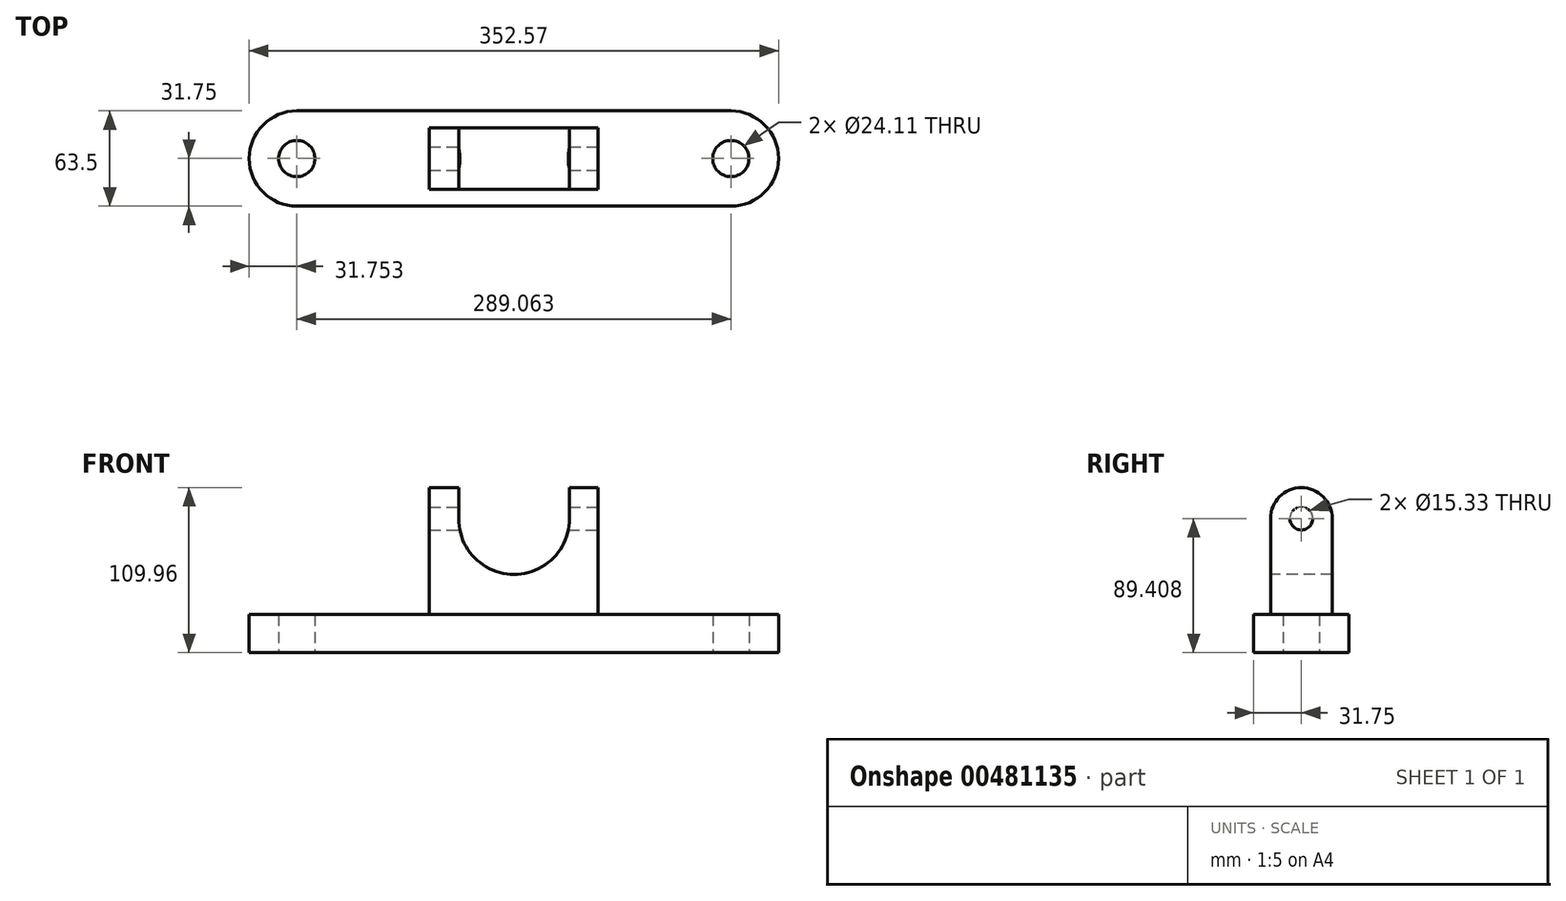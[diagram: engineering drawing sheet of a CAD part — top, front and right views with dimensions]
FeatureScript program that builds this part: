
annotation { "Feature Type Name" : "Feature", "Feature Type Description" : "" }
export const myFeature = defineFeature(function(context is Context, id is Id, definition is map)
    precondition{}
    {
        {
            var Q0;
            Q0=qCreatedBy(makeId("Top.planeOp"),FACE);
            var sketch = newSketch(context, id + "F0", { "sketchPlane" : qUnion([Q0])});
            skArc(sketch, "E0", {"start": v(-144.33, 31.75) * mm, "mid": v(-176.08, 0) * mm, "end": v(-144.33, -31.75) * mm});
            skCircle(sketch, "E1", {"center": v(-144.33, 0) * mm, "radius": 12.05 * mm});
            skArc(sketch, "E2", {"start": v(144.74, -31.75) * mm, "mid": v(176.49, 0) * mm, "end": v(144.74, 31.75) * mm});
            skCircle(sketch, "E3", {"center": v(144.74, 0) * mm, "radius": 12.05 * mm});
            skLineSegment(sketch, "E4", {"start": v(-144.33, 31.75) * mm, "end": v(144.74, 31.75) * mm});
            skLineSegment(sketch, "E5", {"start": v(-144.33, -31.75) * mm, "end": v(144.74, -31.75) * mm});
            skSolve(sketch);
        }
        {
            var Q0;
            Q0=qCreatedBy(makeId("Top.planeOp"),FACE);
            var sketch = newSketch(context, id + "F1", { "sketchPlane" : qUnion([Q0])});
            skLineSegment(sketch, "E6.bottom", {"start": v(56.16, -20.55) * mm, "end": v(-56.16, -20.55) * mm});
            skLineSegment(sketch, "E6.top", {"start": v(56.16, 20.55) * mm, "end": v(-56.16, 20.55) * mm});
            skLineSegment(sketch, "E6.left", {"start": v(56.16, -20.55) * mm, "end": v(56.16, 20.55) * mm});
            skLineSegment(sketch, "E6.right", {"start": v(-56.16, -20.55) * mm, "end": v(-56.16, 20.55) * mm});
            skPoint(sketch, "E6.middle", {"position": v(0, 0) * mm});
            skSolve(sketch);
        }
        {
            var Q0;
            Q0 = qSketchRegion(id + "F1", true);
            extrude(context, id + "F2", {"entities" : qUnion([Q0]), "depth" : 89.4 * mm});
        }
        {
            var Q0;
            Q0 = qSketchRegion(id + "F0", true);
            extrude(context, id + "F3", {"entities" : qUnion([Q0]), "operationType" : NewBodyOperationType.ADD, "depth" : 25.4 * mm});
        }
        {
            var Q0;
            Q0=makeQuery(id+"F2.opExtrude","SWEPT_FACE",FACE,{"disambiguationData":[OSD([sQuery(id+"F1.wireOp",EDGE,"E6.right")])]});
            var sketch = newSketch(context, id + "F4", { "sketchPlane" : qUnion([Q0])});
            skArc(sketch, "E7", {"start": v(20.55, 89.4) * mm, "mid": v(0, 109.96) * mm, "end": v(-20.55, 89.4) * mm});
            skSolve(sketch);
        }
        {
            var Q0;
            Q0=makeQuery(id+"F4.imprint","IMPRINT",FACE,{"disambiguationData":[TD([[makeQuery(id+"F4.imprint","IMPRINT",EDGE,{"derivedFrom":sQuery(id+"F4.wireOp",EDGE,"E7")}),1.0]])]});
            extrude(context, id + "F5", {"entities" : qUnion([Q0]), "operationType" : NewBodyOperationType.ADD, "oppositeDirection" : true, "depth" : 112.32 * mm});
        }
        {
            var Q0;
            Q0=makeQuery(id+"F2.opExtrude","SWEPT_FACE",FACE,{"disambiguationData":[OSD([sQuery(id+"F1.wireOp",EDGE,"E6.left")])]});
            var sketch = newSketch(context, id + "F6", { "sketchPlane" : qUnion([Q0])});
            skCircle(sketch, "E8", {"center": v(0, 89.4) * mm, "radius": 7.66 * mm});
            skSolve(sketch);
        }
        {
            var Q0;
            Q0 = qSketchRegion(id + "F6", true);
            extrude(context, id + "F7", {"entities" : qUnion([Q0]), "operationType" : NewBodyOperationType.REMOVE, "oppositeDirection" : true, "depth" : 308.86 * mm});
        }
        {
            var Q0;
            Q0=makeQuery(id+"F5.opExtrude","CAP_FACE",FACE,{"disambiguationData":[OSD([sQuery(id+"F1.wireOp",EDGE,"E6.right"),sQuery(id+"F4.wireOp",EDGE,"E7")])],"isStart":false});
            var sketch = newSketch(context, id + "F8", { "sketchPlane" : qUnion([Q0])});
            skCircle(sketch, "E9", {"center": v(0, 89.4) * mm, "radius": 7.67 * mm});
            skSolve(sketch);
        }
        {
            var Q0;
            Q0 = qSketchRegion(id + "F8", true);
            extrude(context, id + "F9", {"entities" : qUnion([Q0]), "operationType" : NewBodyOperationType.REMOVE, "oppositeDirection" : true, "depth" : 226.82 * mm});
        }
        {
            var Q0;
            Q0=makeQuery(id+"F2.opExtrude","SWEPT_FACE",FACE,{"disambiguationData":[OSD([sQuery(id+"F1.wireOp",EDGE,"E6.bottom")])]});
            var sketch = newSketch(context, id + "F10", { "sketchPlane" : qUnion([Q0])});
            skArc(sketch, "E10", {"start": v(-36.55, 89.4) * mm, "mid": v(0.32, 52.24) * mm, "end": v(37.2, 89.4) * mm});
            skLineSegment(sketch, "E11", {"start": v(-36.55, 89.4) * mm, "end": v(-36.55, 112.7) * mm});
            skLineSegment(sketch, "E12", {"start": v(37.2, 89.4) * mm, "end": v(37.01, 112.7) * mm});
            skLineSegment(sketch, "E13", {"start": v(-36.55, 112.7) * mm, "end": v(37.01, 112.7) * mm});
            skSolve(sketch);
        }
        {
            var Q0;
            Q0 = qSketchRegion(id + "F10", true);
            extrude(context, id + "F11", {"entities" : qUnion([Q0]), "operationType" : NewBodyOperationType.REMOVE, "oppositeDirection" : true, "depth" : 46.74 * mm});
        }
    });
